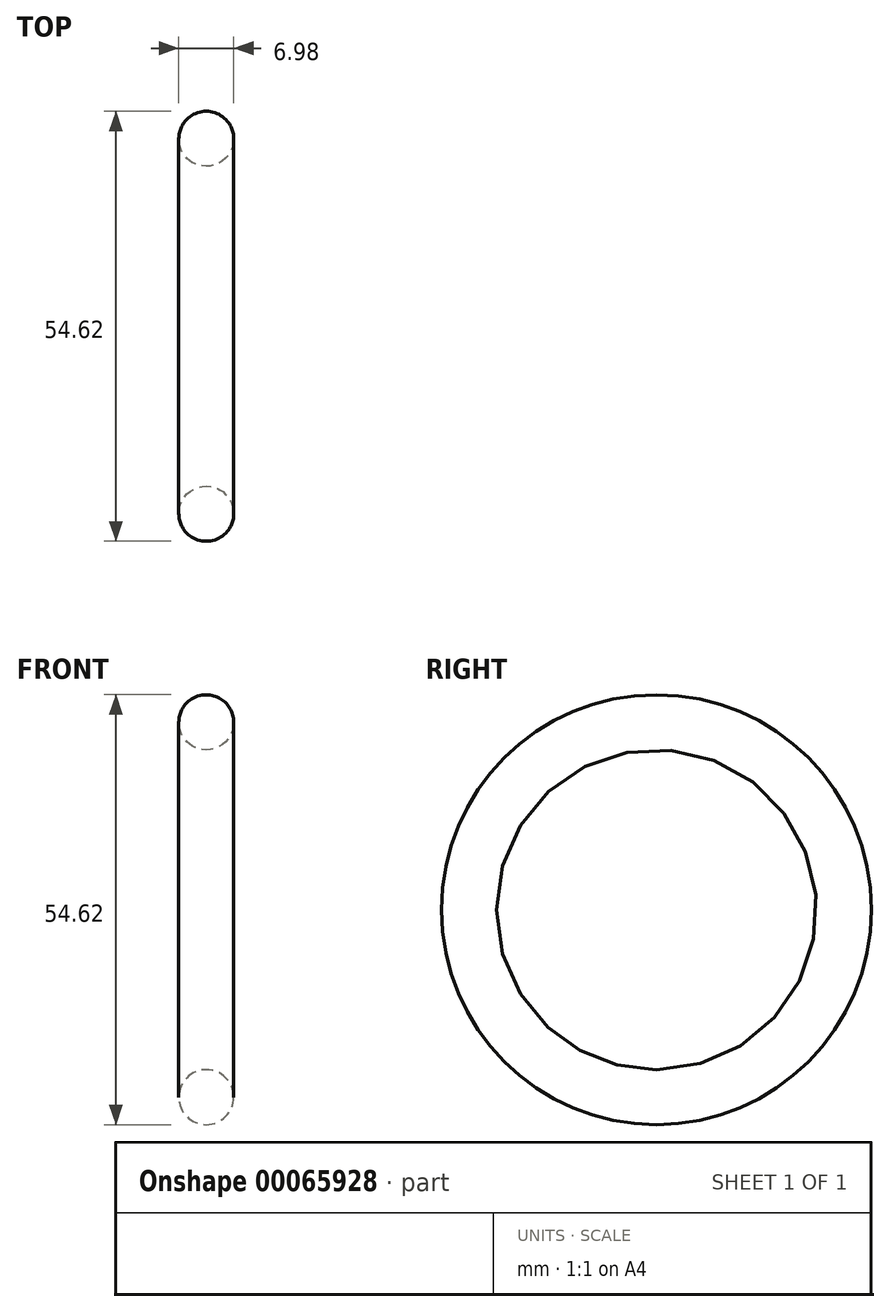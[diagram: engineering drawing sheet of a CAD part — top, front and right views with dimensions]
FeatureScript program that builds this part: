
annotation { "Feature Type Name" : "Feature", "Feature Type Description" : "" }
export const myFeature = defineFeature(function(context is Context, id is Id, definition is map)
    precondition{}
    {
        {
            var Q0;
            Q0=qCreatedBy(makeId("Front.planeOp"),FACE);
            var sketch = newSketch(context, id + "F0", { "sketchPlane" : qUnion([Q0])});
            skLineSegment(sketch, "E0", {"start": v(0, 0) * mm, "end": v(-6.06, 0) * mm, "construction": true});
            skCircle(sketch, "E1", {"center": v(0, 23.81) * mm, "radius": 3.5 * mm});
            skSolve(sketch);
        }
        {
            var Q0;
            Q0=makeQuery(id+"F0.imprint","IMPRINT",FACE,{"disambiguationData":[TD([[makeQuery(id+"F0.imprint","IMPRINT",EDGE,{"derivedFrom":sQuery(id+"F0.wireOp",EDGE,"E1")}),1.0]])]});
            var Q1;
            Q1=sQuery(id+"F0.wireOp",EDGE,"E0");
            revolve(context, id + "F1", {"entities" : qUnion([Q0]), "axis" : qUnion([Q1]), "revolveType" : RevolveType.FULL});
        }
    });
